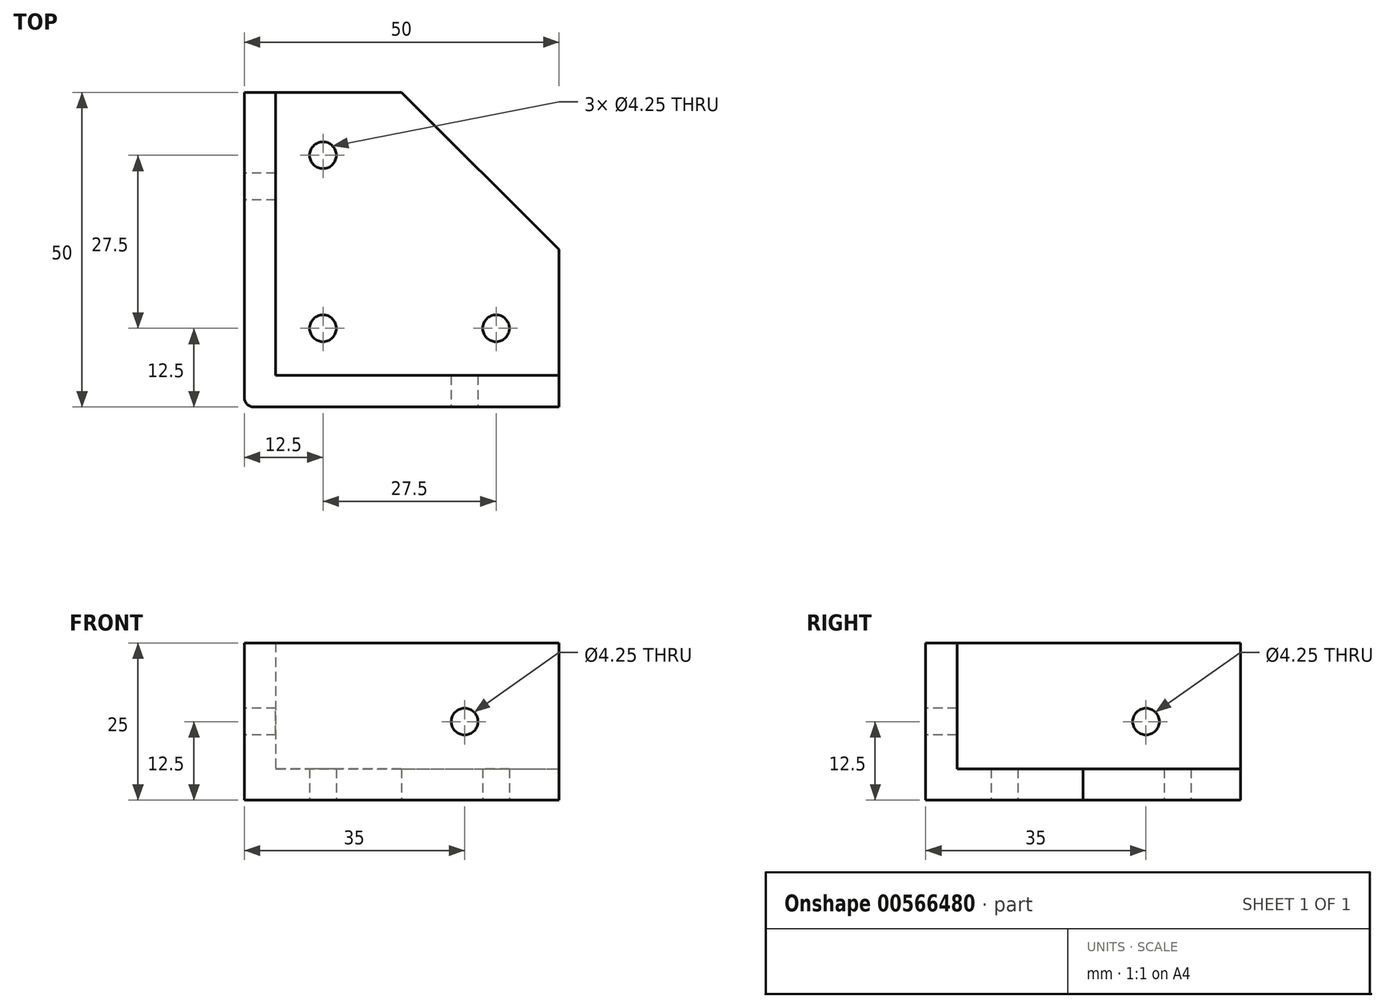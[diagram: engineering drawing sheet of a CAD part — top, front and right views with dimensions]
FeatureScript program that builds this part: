
annotation { "Feature Type Name" : "Feature", "Feature Type Description" : "" }
export const myFeature = defineFeature(function(context is Context, id is Id, definition is map)
    precondition{}
    {
        {
            var Q0;
            Q0=qCreatedBy(makeId("Top.planeOp"),FACE);
            var sketch = newSketch(context, id + "F0", { "sketchPlane" : qUnion([Q0])});
            skLineSegment(sketch, "E0", {"start": v(0, 50) * mm, "end": v(-25, 50) * mm});
            skLineSegment(sketch, "E1", {"start": v(-25, 50) * mm, "end": v(-25, 0) * mm});
            skLineSegment(sketch, "E2", {"start": v(-25, 0) * mm, "end": v(25, 0) * mm});
            skLineSegment(sketch, "E3", {"start": v(25, 0) * mm, "end": v(25, 25) * mm});
            skLineSegment(sketch, "E4", {"start": v(25, 25) * mm, "end": v(0, 25) * mm});
            skLineSegment(sketch, "E5", {"start": v(0, 25) * mm, "end": v(0, 50) * mm});
            skCircle(sketch, "E6", {"center": v(-12.5, 40) * mm, "radius": 2.12 * mm});
            skCircle(sketch, "E7", {"center": v(15, 12.5) * mm, "radius": 2.12 * mm});
            skCircle(sketch, "E8", {"center": v(-12.5, 12.5) * mm, "radius": 2.12 * mm});
            skSolve(sketch);
        }
        {
            var Q0;
            Q0=qSketchRegion(id+"F0",true);
            extrude(context, id + "F1", {"entities" : qUnion([Q0]), "depth" : 5 * mm});
        }
        {
            var Q0;
            Q0=makeQuery(id+"F1.opExtrude","CAP_FACE",FACE,{"disambiguationData":[OSD([sQuery(id+"F0.wireOp",EDGE,"E0"),sQuery(id+"F0.wireOp",EDGE,"E1"),sQuery(id+"F0.wireOp",EDGE,"E2"),sQuery(id+"F0.wireOp",EDGE,"E3"),sQuery(id+"F0.wireOp",EDGE,"E4"),sQuery(id+"F0.wireOp",EDGE,"E5"),sQuery(id+"F0.wireOp",EDGE,"E6"),sQuery(id+"F0.wireOp",EDGE,"E7")])],"isStart":false});
            var sketch = newSketch(context, id + "F2", { "sketchPlane" : qUnion([Q0])});
            skLineSegment(sketch, "E9", {"start": v(-20, 5) * mm, "end": v(25, 5) * mm});
            skLineSegment(sketch, "E10", {"start": v(25, 5) * mm, "end": v(25, 0) * mm});
            skLineSegment(sketch, "E11", {"start": v(25, 0) * mm, "end": v(-25, 0) * mm});
            skLineSegment(sketch, "E12", {"start": v(-25, 5) * mm, "end": v(-25, 0) * mm, "construction": true});
            skLineSegment(sketch, "E13.bottom", {"start": v(-25, 50) * mm, "end": v(-20, 50) * mm});
            skLineSegment(sketch, "E13.top", {"start": v(-25, 0) * mm, "end": v(-20, 0) * mm});
            skLineSegment(sketch, "E13.left", {"start": v(-25, 50) * mm, "end": v(-25, 0) * mm});
            skLineSegment(sketch, "E13.right", {"start": v(-20, 50) * mm, "end": v(-20, 5) * mm});
            skSolve(sketch);
        }
        {
            var Q0;
            Q0=qSketchRegion(id+"F2",true);
            extrude(context, id + "F3", {"entities" : qUnion([Q0]), "operationType" : NewBodyOperationType.ADD, "depth" : 20 * mm});
        }
        {
            var Q0;
            Q0=makeQuery(id+"F76PTgu7nN6sp4q_1.boolean.opBoolean","MERGE",FACE,{"derivedFrom":[makeQuery(id+"F3.boolean.opBoolean","MERGE",FACE,{"derivedFrom":[makeQuery(id+"F1.opExtrude","SWEPT_FACE",FACE,{"disambiguationData":[OSD([sQuery(id+"F0.wireOp",EDGE,"E2")])]}),makeQuery(id+"F3.opExtrude","SWEPT_FACE",FACE,{"disambiguationData":[OSD([sQuery(id+"F2.wireOp",EDGE,"E11")])]})]}),makeQuery(id+"F76PTgu7nN6sp4q_1.opExtrude","SWEPT_FACE",FACE,{"disambiguationData":[OSD([sQuery(id+"FVZp2BhR3DRSIo4_1.wireOp",EDGE,"PXxosK55-A00r-EiAo-lVqn-v3T7ZulwWpec")])]})]});
            var sketch = newSketch(context, id + "F4", { "sketchPlane" : qUnion([Q0])});
            skCircle(sketch, "E14", {"center": v(10, 12.5) * mm, "radius": 2.12 * mm});
            skSolve(sketch);
        }
        {
            var Q0;
            Q0=qSketchRegion(id+"F4",true);
            extrude(context, id + "F5", {"entities" : qUnion([Q0]), "operationType" : NewBodyOperationType.REMOVE, "oppositeDirection" : true, "depth" : 5 * mm});
        }
        {
            var Q0;
            Q0=qCreatedBy(makeId("Top.planeOp"),FACE);
            var sketch = newSketch(context, id + "F6", { "sketchPlane" : qUnion([Q0])});
            skLineSegment(sketch, "E15", {"start": v(0, 50) * mm, "end": v(25, 25) * mm});
            skLineSegment(sketch, "E16", {"start": v(25, 25) * mm, "end": v(0, 25) * mm});
            skLineSegment(sketch, "E17", {"start": v(0, 25) * mm, "end": v(0, 50) * mm});
            skSolve(sketch);
        }
        {
            var Q0;
            Q0=qSketchRegion(id+"F6",true);
            extrude(context, id + "F7", {"entities" : qUnion([Q0]), "operationType" : NewBodyOperationType.ADD, "depth" : 5 * mm});
        }
        {
            var Q0;
            Q0=makeQuery(id+"F3.boolean.opBoolean","MERGE",EDGE,{"derivedFrom":[makeQuery(id+"F1.opExtrude","SWEPT_EDGE",EDGE,{"disambiguationData":[OSD([sQuery(id+"F0.wireOp",EDGE,"E1"),sQuery(id+"F0.wireOp",EDGE,"E2")])]}),makeQuery(id+"F3.opExtrude","SWEPT_EDGE",EDGE,{"disambiguationData":[OSD([sQuery(id+"F2.wireOp",EDGE,"E13.top"),sQuery(id+"F2.wireOp",EDGE,"E13.left")])]})]});
            fillet(context, id + "F8", {"entities" : qUnion([Q0]), "radius" : 1.5 * mm, "tangentPropagation" : true, "allowEdgeOverflow" : false});
        }
        {
            var Q0;
            Q0=makeQuery(id+"F3.boolean.opBoolean","MERGE",FACE,{"derivedFrom":[makeQuery(id+"F1.opExtrude","SWEPT_FACE",FACE,{"disambiguationData":[OSD([sQuery(id+"F0.wireOp",EDGE,"E1")])]}),makeQuery(id+"F3.opExtrude","SWEPT_FACE",FACE,{"disambiguationData":[OSD([sQuery(id+"F2.wireOp",EDGE,"E13.left")])]})]});
            var sketch = newSketch(context, id + "F9", { "sketchPlane" : qUnion([Q0])});
            skCircle(sketch, "E18", {"center": v(-35, 12.5) * mm, "radius": 2.12 * mm});
            skSolve(sketch);
        }
        {
            var Q0;
            Q0=qSketchRegion(id+"F9",true);
            extrude(context, id + "F10", {"entities" : qUnion([Q0]), "operationType" : NewBodyOperationType.REMOVE, "oppositeDirection" : true, "depth" : 25 * mm});
        }
    });
